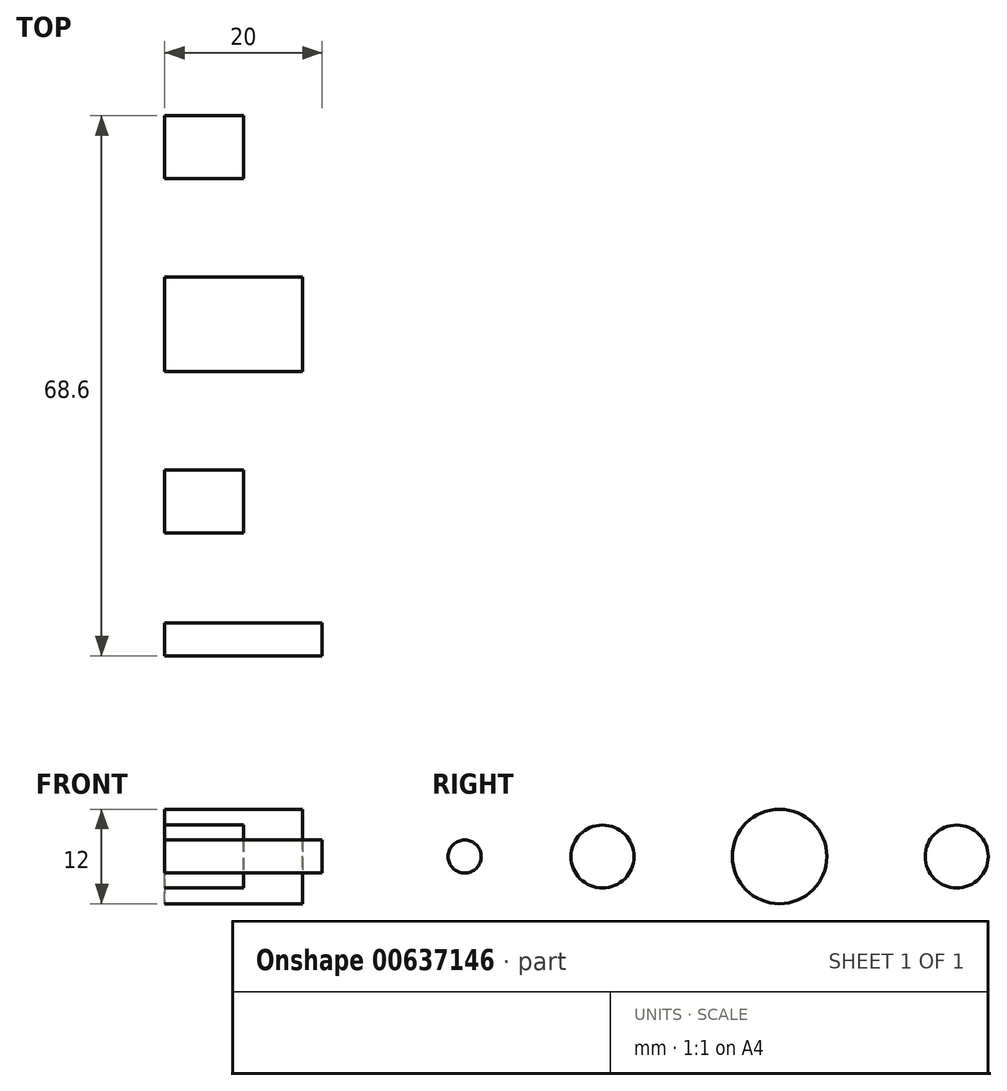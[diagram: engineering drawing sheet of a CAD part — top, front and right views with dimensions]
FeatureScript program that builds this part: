
annotation { "Feature Type Name" : "Feature", "Feature Type Description" : "" }
export const myFeature = defineFeature(function(context is Context, id is Id, definition is map)
    precondition{}
    {
        {
            var Q0;
            Q0=qCreatedBy(makeId("Top.planeOp"),FACE);
            var sketch = newSketch(context, id + "F0", { "sketchPlane" : qUnion([Q0])});
            skLineSegment(sketch, "E0.bottom", {"start": v(10, -50) * mm, "end": v(-10, -50) * mm});
            skLineSegment(sketch, "E0.top", {"start": v(10, 50) * mm, "end": v(-10, 50) * mm});
            skLineSegment(sketch, "E0.left", {"start": v(10, -50) * mm, "end": v(10, 50) * mm});
            skLineSegment(sketch, "E0.right", {"start": v(-10, -50) * mm, "end": v(-10, 50) * mm});
            skPoint(sketch, "E0.middle", {"position": v(0, 0) * mm});
            skSolve(sketch);
        }
        {
            var Q0;
            Q0=makeQuery(id+"F0.imprint","IMPRINT",FACE,{"disambiguationData":[TD([[makeQuery(id+"F0.imprint","IMPRINT",EDGE,{"derivedFrom":sQuery(id+"F0.wireOp",EDGE,"E0.bottom")}),-1.0]])]});
            extrude(context, id + "F1", {"entities" : qUnion([Q0]), "depth" : 20 * mm, "offsetDistance" : 25 * mm});
        }
        {
            var Q0;
            Q0=makeQuery(id+"F1.opExtrude","SWEPT_FACE",FACE,{"disambiguationData":[OSD([sQuery(id+"F0.wireOp",EDGE,"E0.left")])]});
            var sketch = newSketch(context, id + "F2", { "sketchPlane" : qUnion([Q0])});
            skLineSegment(sketch, "E1", {"start": v(50, 10) * mm, "end": v(-50, 10) * mm, "construction": true});
            skCircle(sketch, "E2", {"center": v(0, 10) * mm, "radius": 6 * mm});
            skSolve(sketch);
        }
        {
            var Q0;
            Q0=makeQuery(id+"F2.imprint","IMPRINT",FACE,{"disambiguationData":[TD([[makeQuery(id+"F2.imprint","IMPRINT",EDGE,{"derivedFrom":sQuery(id+"F2.wireOp",EDGE,"E2")}),1.0]])]});
            extrude(context, id + "F3", {"entities" : qUnion([Q0]), "operationType" : NewBodyOperationType.REMOVE, "oppositeDirection" : true, "depth" : 2.5 * mm, "offsetDistance" : 25 * mm});
        }
        {
            var Q0;
            Q0=makeQuery(id+"F1.opExtrude","SWEPT_FACE",FACE,{"disambiguationData":[OSD([sQuery(id+"F0.wireOp",EDGE,"E0.left")])]});
            var sketch = newSketch(context, id + "F4", { "sketchPlane" : qUnion([Q0])});
            skLineSegment(sketch, "E3", {"start": v(50, 10) * mm, "end": v(-50, 10) * mm, "construction": true});
            skCircle(sketch, "E4", {"center": v(22.5, 10) * mm, "radius": 4 * mm});
            skCircle(sketch, "E5", {"center": v(-22.5, 10) * mm, "radius": 4 * mm});
            skSolve(sketch);
        }
        {
            var Q0;
            Q0=makeQuery(id+"F4.imprint","IMPRINT",FACE,{"disambiguationData":[TD([[makeQuery(id+"F4.imprint","IMPRINT",EDGE,{"derivedFrom":sQuery(id+"F4.wireOp",EDGE,"E4")}),1.0]])]});
            var Q1;
            Q1=makeQuery(id+"F4.imprint","IMPRINT",FACE,{"disambiguationData":[TD([[makeQuery(id+"F4.imprint","IMPRINT",EDGE,{"derivedFrom":sQuery(id+"F4.wireOp",EDGE,"E5")}),1.0]])]});
            extrude(context, id + "F5", {"entities" : qUnion([Q0, Q1]), "operationType" : NewBodyOperationType.REMOVE, "oppositeDirection" : true, "depth" : 10 * mm, "offsetDistance" : 25 * mm});
        }
        {
            var Q0;
            Q0=makeQuery(id+"F1.opExtrude","SWEPT_FACE",FACE,{"disambiguationData":[OSD([sQuery(id+"F0.wireOp",EDGE,"E0.left")])]});
            var sketch = newSketch(context, id + "F6", { "sketchPlane" : qUnion([Q0])});
            skLineSegment(sketch, "E6", {"start": v(-50, 10) * mm, "end": v(50, 10) * mm});
            skCircle(sketch, "E7", {"center": v(-40, 10) * mm, "radius": 2.1 * mm});
            skCircle(sketch, "E8", {"center": v(40, 10) * mm, "radius": 2.1 * mm});
            skSolve(sketch);
        }
        {
            var Q0;
            {var subQ0=sQuery(id+"F6.wireOp",EDGE,"E7");var subQ1=sQuery(id+"F6.wireOp",EDGE,"E6");var subQ2=makeQuery(id+"F6.imprint","INTERSECT",VERTEX,{"disambiguationData":[OD(0.0)],"derivedFrom":[subQ1,subQ0]});Q0=makeQuery(id+"F6.imprint","IMPRINT",FACE,{"disambiguationData":[TD([[makeQuery(id+"F6.imprint","IMPRINT",EDGE,{"disambiguationData":[TD([[subQ2,-1.0]])],"derivedFrom":subQ1}),1.0]])]});}
            var Q1;
            {var subQ0=sQuery(id+"F6.wireOp",EDGE,"E7");var subQ1=sQuery(id+"F6.wireOp",EDGE,"E6");var subQ2=makeQuery(id+"F6.imprint","INTERSECT",VERTEX,{"disambiguationData":[OD(0.0)],"derivedFrom":[subQ1,subQ0]});Q1=makeQuery(id+"F6.imprint","IMPRINT",FACE,{"disambiguationData":[TD([[makeQuery(id+"F6.imprint","IMPRINT",EDGE,{"disambiguationData":[TD([[subQ2,-1.0]])],"derivedFrom":subQ1}),-1.0]])]});}
            var Q2;
            {var subQ0=sQuery(id+"F6.wireOp",EDGE,"E8");var subQ1=sQuery(id+"F6.wireOp",EDGE,"E6");var subQ2=makeQuery(id+"F6.imprint","INTERSECT",VERTEX,{"disambiguationData":[OD(0.0)],"derivedFrom":[subQ1,subQ0]});Q2=makeQuery(id+"F6.imprint","IMPRINT",FACE,{"disambiguationData":[TD([[makeQuery(id+"F6.imprint","IMPRINT",EDGE,{"disambiguationData":[TD([[subQ2,-1.0]])],"derivedFrom":subQ1}),-1.0]])]});}
            var Q3;
            {var subQ0=sQuery(id+"F6.wireOp",EDGE,"E8");var subQ1=sQuery(id+"F6.wireOp",EDGE,"E6");var subQ2=makeQuery(id+"F6.imprint","INTERSECT",VERTEX,{"disambiguationData":[OD(0.0)],"derivedFrom":[subQ1,subQ0]});Q3=makeQuery(id+"F6.imprint","IMPRINT",FACE,{"disambiguationData":[TD([[makeQuery(id+"F6.imprint","IMPRINT",EDGE,{"disambiguationData":[TD([[subQ2,-1.0]])],"derivedFrom":subQ1}),1.0]])]});}
            extrude(context, id + "F7", {"entities" : qUnion([Q0, Q1, Q2, Q3]), "operationType" : NewBodyOperationType.REMOVE, "oppositeDirection" : true, "depth" : 25 * mm, "offsetDistance" : 25 * mm});
        }
    });
